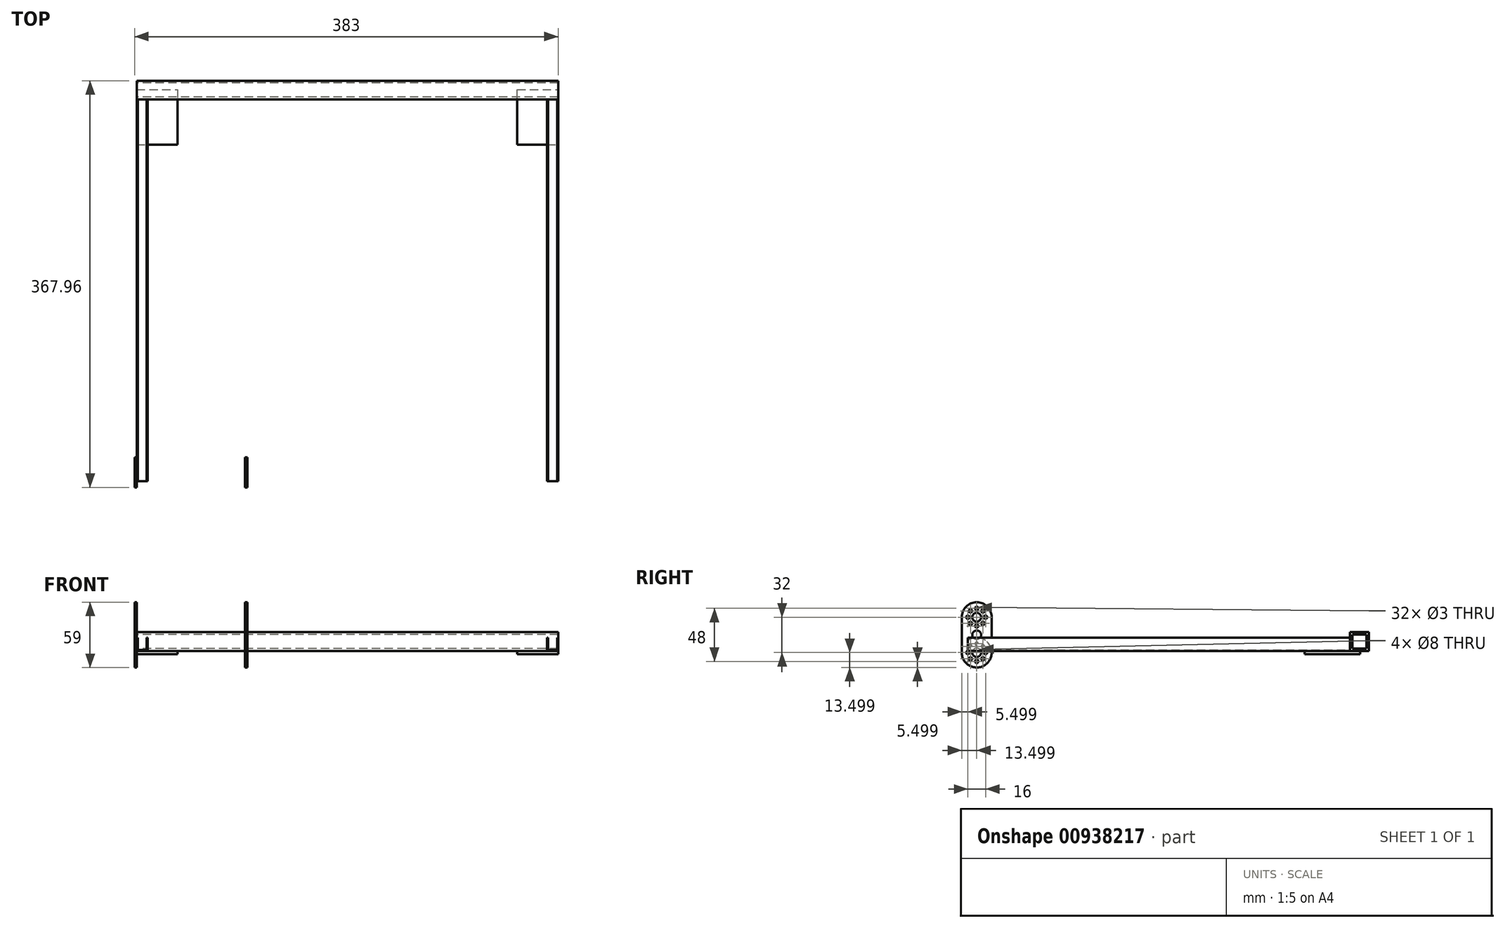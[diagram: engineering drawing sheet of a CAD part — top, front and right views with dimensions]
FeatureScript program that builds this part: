
annotation { "Feature Type Name" : "Feature", "Feature Type Description" : "" }
export const myFeature = defineFeature(function(context is Context, id is Id, definition is map)
    precondition{}
    {
        {
            var Q0;
            Q0=qCreatedBy(makeId("Right.planeOp"),FACE);
            var sketch = newSketch(context, id + "F0", { "sketchPlane" : qUnion([Q0])});
            skLineSegment(sketch, "E0.bottom", {"start": v(8.5, 8.5) * mm, "end": v(-8.5, 8.5) * mm});
            skLineSegment(sketch, "E0.top", {"start": v(8.5, -8.5) * mm, "end": v(-8.5, -8.5) * mm});
            skLineSegment(sketch, "E0.left", {"start": v(8.5, 8.5) * mm, "end": v(8.5, -8.5) * mm});
            skLineSegment(sketch, "E0.right", {"start": v(-8.5, 8.5) * mm, "end": v(-8.5, -8.5) * mm});
            skPoint(sketch, "E0.middle", {"position": v(0, 0) * mm});
            skLineSegment(sketch, "E1.bottom", {"start": v(6.35, 6.35) * mm, "end": v(-6.35, 6.35) * mm});
            skLineSegment(sketch, "E1.top", {"start": v(6.35, -6.35) * mm, "end": v(-6.35, -6.35) * mm});
            skLineSegment(sketch, "E1.left", {"start": v(6.35, 6.35) * mm, "end": v(6.35, -6.35) * mm});
            skLineSegment(sketch, "E1.right", {"start": v(-6.35, 6.35) * mm, "end": v(-6.35, -6.35) * mm});
            skSolve(sketch);
        }
        {
            var Q0;
            Q0=makeQuery(id+"F0.imprint","IMPRINT",FACE,{"disambiguationData":[TD([[makeQuery(id+"F0.imprint","IMPRINT",EDGE,{"derivedFrom":sQuery(id+"F0.wireOp",EDGE,"E0.bottom")}),1.0]])]});
            extrude(context, id + "F1", {"entities" : qUnion([Q0]), "depth" : 381 * mm, "offsetDistance" : 25 * mm});
        }
        {
            var Q0;
            Q0=makeQuery(id+"F1.opExtrude","SWEPT_FACE",FACE,{"disambiguationData":[OSD([sQuery(id+"F0.wireOp",EDGE,"E0.right")])]});
            var sketch = newSketch(context, id + "F2", { "sketchPlane" : qUnion([Q0])});
            skLineSegment(sketch, "E2.bottom", {"start": v(0, -8.5) * mm, "end": v(10, -8.5) * mm});
            skLineSegment(sketch, "E2.top", {"start": v(0, 3.5) * mm, "end": v(10, 3.5) * mm});
            skLineSegment(sketch, "E2.left", {"start": v(0, -8.5) * mm, "end": v(0, 3.5) * mm});
            skLineSegment(sketch, "E2.right", {"start": v(10, -8.5) * mm, "end": v(10, 3.5) * mm});
            skLineSegment(sketch, "E3.bottom", {"start": v(1, 3.5) * mm, "end": v(9, 3.5) * mm});
            skLineSegment(sketch, "E3.top", {"start": v(1, -7.5) * mm, "end": v(9, -7.5) * mm});
            skLineSegment(sketch, "E3.left", {"start": v(1, 3.5) * mm, "end": v(1, -7.5) * mm});
            skLineSegment(sketch, "E3.right", {"start": v(9, 3.5) * mm, "end": v(9, -7.5) * mm});
            skSolve(sketch);
        }
        {
            var Q0;
            Q0=makeQuery(id+"F2.imprint","IMPRINT",FACE,{"disambiguationData":[TD([[makeQuery(id+"F2.imprint","IMPRINT",EDGE,{"derivedFrom":sQuery(id+"F2.wireOp",EDGE,"E2.bottom")}),-1.0]])]});
            extrude(context, id + "F3", {"entities" : qUnion([Q0]), "depth" : 345.44 * mm, "offsetDistance" : 25 * mm});
        }
        {
            var Q0;
            Q0=makeQuery(id+"F3.opExtrude","SWEPT_BODY",BODY,{"disambiguationData":[OSD([sQuery(id+"F2.wireOp",EDGE,"E2.bottom"),sQuery(id+"F2.wireOp",EDGE,"E2.top"),sQuery(id+"F2.wireOp",EDGE,"E2.left"),sQuery(id+"F2.wireOp",EDGE,"E2.right"),sQuery(id+"F2.wireOp",EDGE,"E3.top"),sQuery(id+"F2.wireOp",EDGE,"E3.left"),sQuery(id+"F2.wireOp",EDGE,"E3.right")])]});
            transform(context, id + "F4", {"entities" : qUnion([Q0]), "transformType" : TransformType.TRANSLATION_3D, "dx" : 371 * mm, "dy" : 0 * mm, "dz" : 0 * mm, "makeCopy" : true});
        }
        {
            var Q0;
            Q0=makeQuery(id+"F1.opExtrude","SWEPT_FACE",FACE,{"disambiguationData":[OSD([sQuery(id+"F0.wireOp",EDGE,"E0.top")])]});
            var sketch = newSketch(context, id + "F5", { "sketchPlane" : qUnion([Q0])});
            skLineSegment(sketch, "E4.bottom", {"start": v(344, 49.5) * mm, "end": v(381, 49.5) * mm});
            skLineSegment(sketch, "E4.top", {"start": v(344, -0.5) * mm, "end": v(381, -0.5) * mm});
            skLineSegment(sketch, "E4.left", {"start": v(344, 49.5) * mm, "end": v(344, -0.5) * mm});
            skLineSegment(sketch, "E4.right", {"start": v(381, 49.5) * mm, "end": v(381, -0.5) * mm});
            skSolve(sketch);
        }
        {
            var Q0;
            {var subQ0=sQuery(id+"F5.wireOp",EDGE,"E4.top");Q0=makeQuery(id+"F5.imprint","IMPRINT",FACE,{"disambiguationData":[TD([[makeQuery(id+"F5.imprint","IMPRINT",EDGE,{"derivedFrom":subQ0}),1.0]])]});}
            var Q1;
            {var subQ0=sQuery(id+"F5.wireOp",EDGE,"E4.bottom");Q1=makeQuery(id+"F5.imprint","IMPRINT",FACE,{"disambiguationData":[TD([[makeQuery(id+"F5.imprint","IMPRINT",EDGE,{"derivedFrom":subQ0}),-1.0]])]});}
            extrude(context, id + "F6", {"entities" : qUnion([Q0, Q1]), "depth" : 3 * mm, "offsetDistance" : 25 * mm});
        }
        {
            var Q0;
            Q0=makeQuery(id+"F6.opExtrude","SWEPT_BODY",BODY,{"disambiguationData":[OSD([sQuery(id+"F5.wireOp",EDGE,"E4.bottom"),sQuery(id+"F5.wireOp",EDGE,"E4.top"),sQuery(id+"F5.wireOp",EDGE,"E4.left"),sQuery(id+"F5.wireOp",EDGE,"E4.right")])]});
            transform(context, id + "F7", {"entities" : qUnion([Q0]), "transformType" : TransformType.TRANSLATION_3D, "dx" : -344 * mm, "dy" : 0 * mm, "dz" : 0 * mm, "makeCopy" : true});
        }
        {
            var Q0;
            Q0=makeQuery(id+"F3.opExtrude","SWEPT_FACE",FACE,{"disambiguationData":[OSD([sQuery(id+"F2.wireOp",EDGE,"E2.left")])]});
            var sketch = newSketch(context, id + "F8", { "sketchPlane" : qUnion([Q0])});
            skCircle(sketch, "E5", {"center": v(345.96, -9.92) * mm, "radius": 13.5 * mm});
            skCircle(sketch, "E6", {"center": v(345.96, 22.08) * mm, "radius": 13.5 * mm});
            skLineSegment(sketch, "E7", {"start": v(332.46, 22.08) * mm, "end": v(332.46, -9.92) * mm});
            skLineSegment(sketch, "E8", {"start": v(359.46, 22.08) * mm, "end": v(359.46, -9.92) * mm});
            skCircle(sketch, "E9", {"center": v(345.96, 22.08) * mm, "radius": 4 * mm});
            skCircle(sketch, "E10", {"center": v(345.96, 30.08) * mm, "radius": 1.5 * mm});
            skPoint(sketch, "E11.center", {"position": v(0, 0) * mm});
            skCircle(sketch, "E12.1.0", {"center": v(340.3, 27.74) * mm, "radius": 1.5 * mm});
            skCircle(sketch, "E12.2.0", {"center": v(337.96, 22.08) * mm, "radius": 1.5 * mm});
            skCircle(sketch, "E12.3.0", {"center": v(340.3, 16.42) * mm, "radius": 1.5 * mm});
            skCircle(sketch, "E12.4.0", {"center": v(345.96, 14.08) * mm, "radius": 1.5 * mm});
            skCircle(sketch, "E12.5.0", {"center": v(351.62, 16.42) * mm, "radius": 1.5 * mm});
            skCircle(sketch, "E12.6.0", {"center": v(353.96, 22.08) * mm, "radius": 1.5 * mm});
            skCircle(sketch, "E12.7.0", {"center": v(351.62, 27.74) * mm, "radius": 1.5 * mm});
            skCircle(sketch, "E13", {"center": v(345.96, -9.92) * mm, "radius": 4 * mm});
            skCircle(sketch, "E14", {"center": v(345.96, -1.92) * mm, "radius": 1.5 * mm});
            skCircle(sketch, "E15.1.0", {"center": v(340.3, -4.26) * mm, "radius": 1.5 * mm});
            skCircle(sketch, "E15.2.0", {"center": v(337.96, -9.92) * mm, "radius": 1.5 * mm});
            skCircle(sketch, "E15.3.0", {"center": v(340.3, -15.58) * mm, "radius": 1.5 * mm});
            skCircle(sketch, "E15.4.0", {"center": v(345.96, -17.92) * mm, "radius": 1.5 * mm});
            skCircle(sketch, "E15.5.0", {"center": v(351.62, -15.58) * mm, "radius": 1.5 * mm});
            skCircle(sketch, "E15.6.0", {"center": v(353.96, -9.92) * mm, "radius": 1.5 * mm});
            skCircle(sketch, "E15.7.0", {"center": v(351.62, -4.26) * mm, "radius": 1.5 * mm});
            skCircle(sketch, "E16", {"center": v(345.96, 6.08) * mm, "radius": 4 * mm});
            skSolve(sketch);
        }
        {
            var Q0;
            {var subQ0=sQuery(id+"F8.wireOp",EDGE,"E7");var subQ1=sQuery(id+"F8.wireOp",EDGE,"E6");var subQ2=makeQuery(id+"F8.imprint","INTERSECT",VERTEX,{"derivedFrom":[subQ1,subQ0]});Q0=makeQuery(id+"F8.imprint","IMPRINT",FACE,{"disambiguationData":[TD([[makeQuery(id+"F8.imprint","IMPRINT",EDGE,{"disambiguationData":[TD([[subQ2,-1.0]])],"derivedFrom":subQ1}),-1.0]])]});}
            var Q1;
            Q1=makeQuery(id+"F8.imprint","IMPRINT",FACE,{"disambiguationData":[TD([[makeQuery(id+"F8.imprint","IMPRINT",EDGE,{"derivedFrom":sQuery(id+"F8.wireOp",EDGE,"E9")}),-1.0]])]});
            var Q2;
            {var subQ1=sQuery(id+"F8.wireOp",EDGE,"E8");Q2=makeQuery(id+"F8.imprint","IMPRINT",FACE,{"disambiguationData":[TD([[makeQuery(id+"F8.imprint","IMPRINT",EDGE,{"derivedFrom":subQ1}),-1.0]])]});}
            var Q3;
            Q3=makeQuery(id+"F8.imprint","IMPRINT",FACE,{"disambiguationData":[TD([[makeQuery(id+"F8.imprint","IMPRINT",EDGE,{"derivedFrom":sQuery(id+"F8.wireOp",EDGE,"E15.3.0")}),-1.0]])]});
            var Q4;
            Q4=makeQuery(id+"F8.imprint","IMPRINT",FACE,{"disambiguationData":[TD([[makeQuery(id+"F8.imprint","IMPRINT",EDGE,{"derivedFrom":sQuery(id+"F8.wireOp",EDGE,"E14")}),-1.0]])]});
            var Q5;
            {var subQ4=sQuery(id+"F8.wireOp",EDGE,"E5");var subQ6=sQuery(id+"F8.wireOp",EDGE,"E16");var subQ7=makeQuery(id+"F8.imprint","INTERSECT",VERTEX,{"disambiguationData":[OD(1.0)],"derivedFrom":[subQ4,subQ6]});Q5=makeQuery(id+"F8.imprint","IMPRINT",FACE,{"disambiguationData":[TD([[makeQuery(id+"F8.imprint","IMPRINT",EDGE,{"disambiguationData":[TD([[subQ7,-1.0]])],"derivedFrom":subQ4}),-1.0]])]});}
            var Q6;
            {var subQ0=sQuery(id+"F8.wireOp",EDGE,"E16");var subQ1=sQuery(id+"F8.wireOp",EDGE,"E5");var subQ2=makeQuery(id+"F8.imprint","INTERSECT",VERTEX,{"disambiguationData":[OD(0.0)],"derivedFrom":[subQ1,subQ0]});Q6=makeQuery(id+"F8.imprint","IMPRINT",FACE,{"disambiguationData":[TD([[makeQuery(id+"F8.imprint","IMPRINT",EDGE,{"disambiguationData":[TD([[subQ2,1.0]])],"derivedFrom":subQ1}),-1.0]])]});}
            extrude(context, id + "F9", {"entities" : qUnion([Q0, Q1, Q2, Q3, Q4, Q5, Q6]), "depth" : 2 * mm, "offsetDistance" : 25 * mm});
        }
        {
            var Q0;
            Q0=makeQuery(id+"F9.opExtrude","SWEPT_BODY",BODY,{"disambiguationData":[OSD([sQuery(id+"F2.wireOp",EDGE,"E2.bottom"),sQuery(id+"F2.wireOp",EDGE,"E2.left"),sQuery(id+"F8.wireOp",EDGE,"E6"),sQuery(id+"F8.wireOp",EDGE,"E7"),sQuery(id+"F8.wireOp",EDGE,"E8"),sQuery(id+"F8.wireOp",EDGE,"E9"),sQuery(id+"F8.wireOp",EDGE,"E10"),sQuery(id+"F8.wireOp",EDGE,"E12.1.0"),sQuery(id+"F8.wireOp",EDGE,"E12.2.0"),sQuery(id+"F8.wireOp",EDGE,"E12.3.0"),sQuery(id+"F8.wireOp",EDGE,"E12.4.0"),sQuery(id+"F8.wireOp",EDGE,"E12.5.0"),sQuery(id+"F8.wireOp",EDGE,"E12.6.0"),sQuery(id+"F8.wireOp",EDGE,"E12.7.0"),sQuery(id+"F8.wireOp",EDGE,"E5"),sQuery(id+"F8.wireOp",EDGE,"E13"),sQuery(id+"F8.wireOp",EDGE,"E14"),sQuery(id+"F8.wireOp",EDGE,"E15.1.0"),sQuery(id+"F8.wireOp",EDGE,"E15.2.0"),sQuery(id+"F8.wireOp",EDGE,"E15.3.0"),sQuery(id+"F8.wireOp",EDGE,"E15.4.0"),sQuery(id+"F8.wireOp",EDGE,"E15.5.0"),sQuery(id+"F8.wireOp",EDGE,"E15.6.0"),sQuery(id+"F8.wireOp",EDGE,"E15.7.0"),sQuery(id+"F8.wireOp",EDGE,"E16")])]});
            transform(context, id + "F10", {"entities" : qUnion([Q0]), "transformType" : TransformType.TRANSLATION_3D, "dx" : 100 * mm, "dy" : 0 * mm, "dz" : 0 * mm, "makeCopy" : true});
        }
    });
